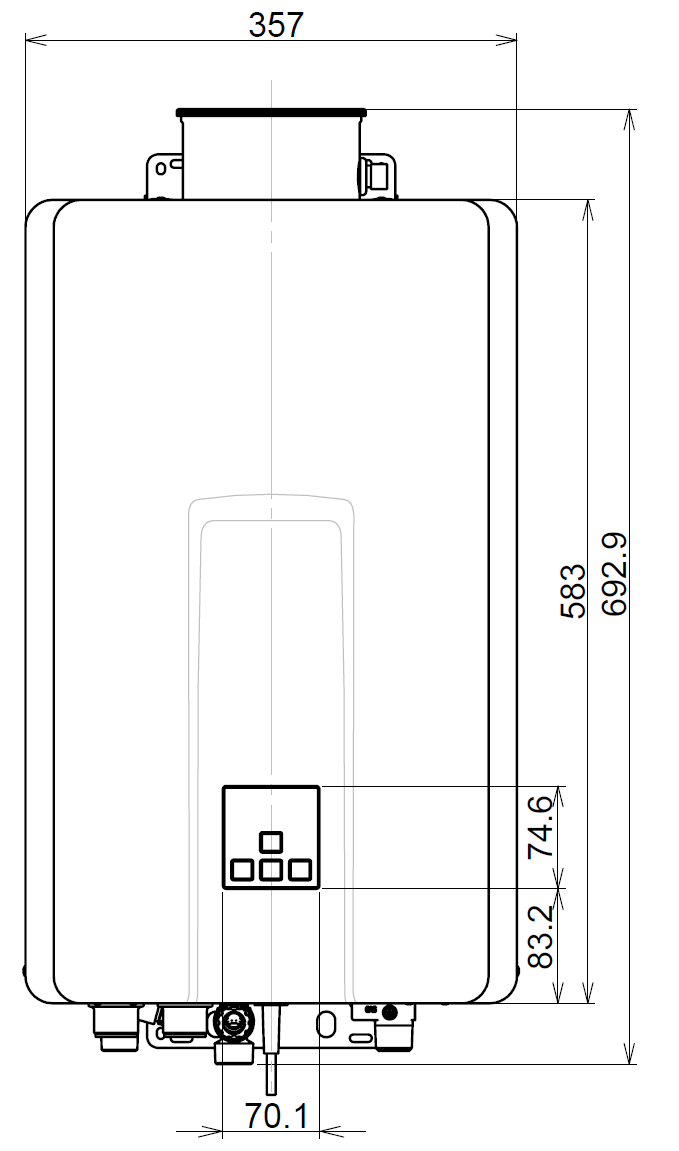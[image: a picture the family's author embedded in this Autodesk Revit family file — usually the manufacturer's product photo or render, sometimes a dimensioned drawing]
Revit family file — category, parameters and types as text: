
# Revit family: hd49i with pipe cover (1)
name_source: partatom
category: Generic Models
units: mm (PartAtom-declared; Revit-internal decimal feet)

## family parameters
Can host rebar = No
Cut with Voids When Loaded = No
Host = Face
Part Type = Normal
Room Calculation Point = No
Round Connector Dimension = Use Diameter
Shared = No

## types (2) — shared parameters
Cold connection from back of unit = 60 mm
Cold connection from centreline = 27 mm
Cold water connection = 20 mm
Cold water inlet = R¾ (20 mm)
Default Elevation = 1219 mm
Efficiency = 82%
Flueing = The internal N49kWi models MUST USE Rinnai flue components—use of non approved flue components will result in a dangerous installation
Gas connection = 20 mm
Gas connection from back of unit = 89 mm
Gas connection from centreline = 89 mm
Gas supply = R¾ (20 mm)
Hot connection from back of unit = 81 mm
Hot connection from centreline = 110 mm  [stored 0.360892 ft]
Hot water capacity = 1.4-37 L/min
Hot water connection = 20 mm
Hot water outlet = R¾ (20 mm)
Ignition system = Direct electronic ignition
Ingress protection rating = IPX2
Input = 11-210 MJ/h
Line pressure maximum = 3.5 kPa (maximum standing pressure under abnormal intermittent conditions is 5.0 kPa).
In the case of commercial metering (i.e. 35-37 kPa coming in), there may be a requirement to regulate the incoming line pressure down
Manufacturer = Rinnai
Minimum water flow = 1.5 L/min
NOx af = 40ppm
Noise level = 54
Nominal operating pressure (water supply) = 200-1000kPa
Nominal water capacity = 28 L/min @25° rise (1680L/h)
Output = 48.8 kW
Power consumption (Normal) = 66 W
Power consumption (antifrost) = 104 W
Power consumption (standby) = 2 W
Type Comments = HD49 units are primarily designed for commercial applications, but can be used for larger hot water capacity residential projects.
Weight = 21 kg

## per-type parameters (varying)
| type | Constraint | Description | Line pressure | Model |
| HD49i (NG) | 1 | HD49 Internal Natural Gas | 1.13-3.0 kPa | HD49iN |
| HD49i (LPG) | 2 | HD49 Internal LPG | 2.75-3.0 kPa | HD49iL |

note: [stored X ft] marks values corroborated as IEEE doubles in the binary element streams (Revit-internal decimal feet)

## geometry (parser evidence)
native form markers: Sweep x1
no freeform markers — native parametric forms only
